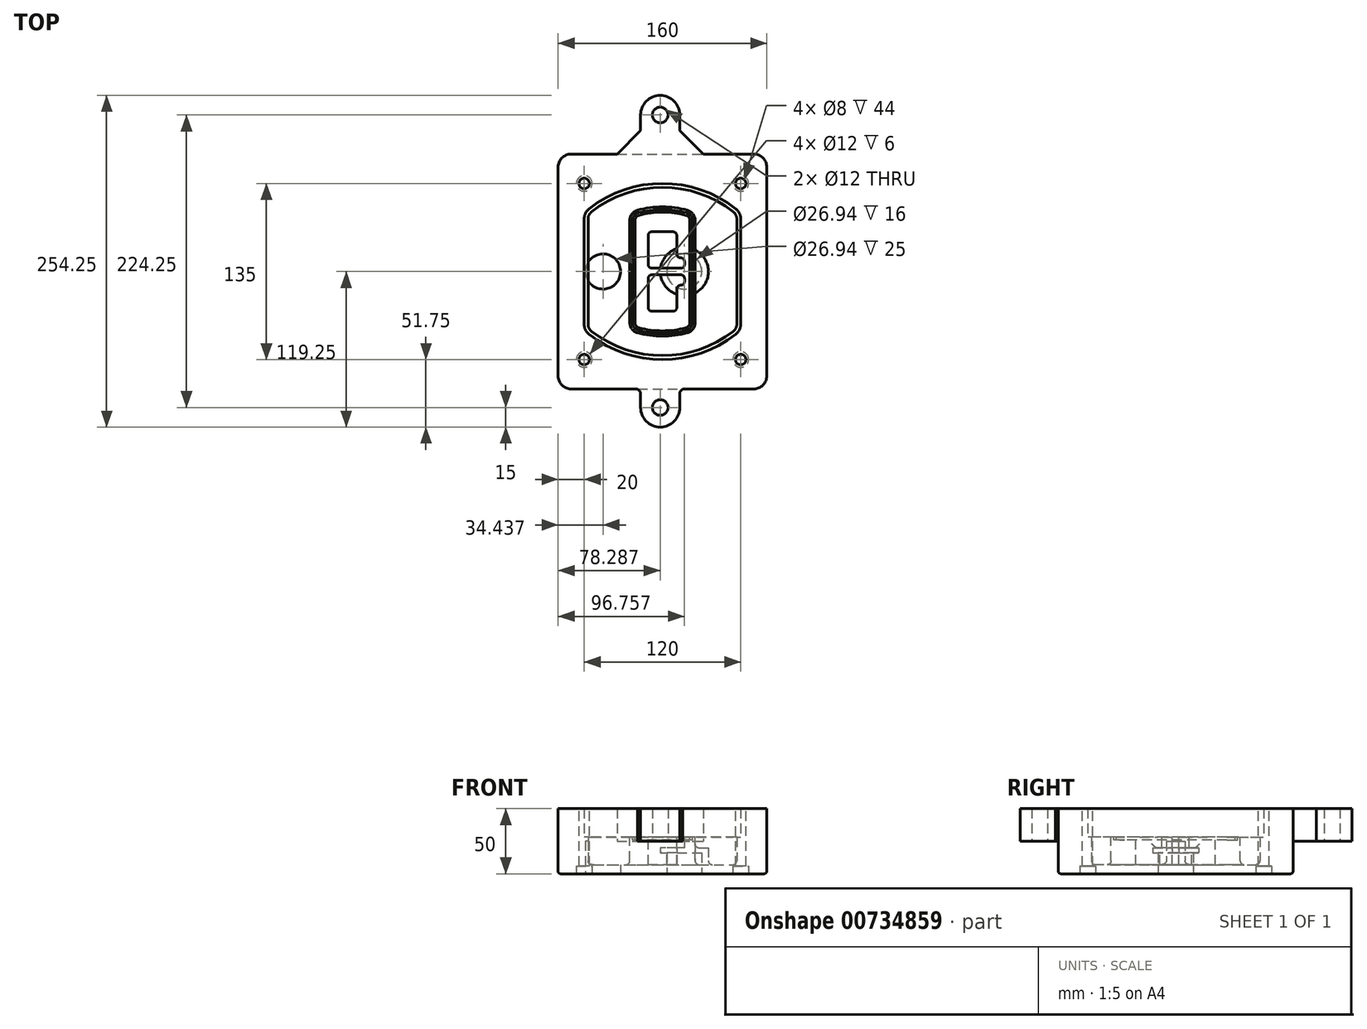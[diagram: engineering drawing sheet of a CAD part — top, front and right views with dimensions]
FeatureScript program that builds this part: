
annotation { "Feature Type Name" : "Feature", "Feature Type Description" : "" }
export const myFeature = defineFeature(function(context is Context, id is Id, definition is map)
    precondition{}
    {
        {
            var Q0;
            Q0=qCreatedBy(makeId("Top.planeOp"),FACE);
            var sketch = newSketch(context, id + "F0", { "sketchPlane" : qUnion([Q0])});
            skPoint(sketch, "E0.rect.middle", {"position": v(0, 0) * mm});
            skLineSegment(sketch, "E1.bottom", {"start": v(-70, -90) * mm, "end": v(70, -90) * mm});
            skLineSegment(sketch, "E1.top", {"start": v(-70, 90) * mm, "end": v(70, 90) * mm});
            skLineSegment(sketch, "E1.left", {"start": v(-80, -80) * mm, "end": v(-80, 80) * mm});
            skLineSegment(sketch, "E1.right", {"start": v(80, -80) * mm, "end": v(80, 80) * mm});
            skLineSegment(sketch, "E2", {"start": v(-80, 90) * mm, "end": v(80, -90) * mm, "construction": true});
            skLineSegment(sketch, "E3", {"start": v(80, 90) * mm, "end": v(-80, -90) * mm, "construction": true});
            skCircle(sketch, "E4", {"center": v(-60, 67.5) * mm, "radius": 4 * mm});
            skCircle(sketch, "E5", {"center": v(60, 67.5) * mm, "radius": 4 * mm});
            skCircle(sketch, "E6", {"center": v(60, -67.5) * mm, "radius": 4 * mm});
            skCircle(sketch, "E7", {"center": v(-60, -67.5) * mm, "radius": 4 * mm});
            skLineSegment(sketch, "E8", {"start": v(-60, 67.5) * mm, "end": v(60, 67.5) * mm, "construction": true});
            skLineSegment(sketch, "E9", {"start": v(60, 67.5) * mm, "end": v(60, -67.5) * mm, "construction": true});
            skLineSegment(sketch, "E10", {"start": v(60, -67.5) * mm, "end": v(-60, -67.5) * mm, "construction": true});
            skLineSegment(sketch, "E11", {"start": v(-60, -67.5) * mm, "end": v(-60, 67.5) * mm, "construction": true});
            skLineSegment(sketch, "E12", {"start": v(-60, 40.3) * mm, "end": v(-60, -40.3) * mm});
            skLineSegment(sketch, "E13", {"start": v(60, 40.3) * mm, "end": v(60, -40.3) * mm});
            skArc(sketch, "E14", {"start": v(56.15, 48.18) * mm, "mid": v(0, 67.5) * mm, "end": v(-56.15, 48.18) * mm});
            skArc(sketch, "E15", {"start": v(-56.15, -48.18) * mm, "mid": v(0, -67.5) * mm, "end": v(56.15, -48.18) * mm});
            skLineSegment(sketch, "E16", {"start": v(-60, 0) * mm, "end": v(60, 0) * mm, "construction": true});
            skPoint(sketch, "E17.visualSharp", {"position": v(-60, -45) * mm});
            skArc(sketch, "E17.filletArc", {"start": v(-60, -40.3) * mm, "mid": v(-58.99, -44.68) * mm, "end": v(-56.15, -48.18) * mm});
            skPoint(sketch, "E18.visualSharp", {"position": v(-60, 45) * mm});
            skArc(sketch, "E18.filletArc", {"start": v(-56.15, 48.18) * mm, "mid": v(-58.99, 44.68) * mm, "end": v(-60, 40.3) * mm});
            skPoint(sketch, "E19.visualSharp", {"position": v(60, 45) * mm});
            skArc(sketch, "E19.filletArc", {"start": v(60, 40.3) * mm, "mid": v(58.99, 44.68) * mm, "end": v(56.15, 48.18) * mm});
            skPoint(sketch, "E20.visualSharp", {"position": v(60, -45) * mm});
            skArc(sketch, "E20.filletArc", {"start": v(56.15, -48.18) * mm, "mid": v(58.99, -44.68) * mm, "end": v(60, -40.3) * mm});
            skPoint(sketch, "E21.visualSharp", {"position": v(-80, 90) * mm});
            skArc(sketch, "E21.filletArc", {"start": v(-70, 90) * mm, "mid": v(-77.07, 87.07) * mm, "end": v(-80, 80) * mm});
            skPoint(sketch, "E22.visualSharp", {"position": v(80, 90) * mm});
            skArc(sketch, "E22.filletArc", {"start": v(80, 80) * mm, "mid": v(77.07, 87.07) * mm, "end": v(70, 90) * mm});
            skPoint(sketch, "E23.visualSharp", {"position": v(80, -90) * mm});
            skArc(sketch, "E23.filletArc", {"start": v(70, -90) * mm, "mid": v(77.07, -87.07) * mm, "end": v(80, -80) * mm});
            skPoint(sketch, "E24.visualSharp", {"position": v(-80, -90) * mm});
            skArc(sketch, "E24.filletArc", {"start": v(-80, -80) * mm, "mid": v(-77.07, -87.07) * mm, "end": v(-70, -90) * mm});
            skArc(sketch, "E25.0", {"start": v(57, 40.3) * mm, "mid": v(56.3, 43.36) * mm, "end": v(54.3, 45.81) * mm});
            skLineSegment(sketch, "E25.1", {"start": v(57, 40.3) * mm, "end": v(57, -40.3) * mm});
            skArc(sketch, "E25.2", {"start": v(54.3, -45.81) * mm, "mid": v(56.3, -43.36) * mm, "end": v(57, -40.3) * mm});
            skArc(sketch, "E25.3", {"start": v(-54.3, -45.81) * mm, "mid": v(0, -64.5) * mm, "end": v(54.3, -45.81) * mm});
            skArc(sketch, "E25.4", {"start": v(-57, -40.3) * mm, "mid": v(-56.3, -43.36) * mm, "end": v(-54.3, -45.81) * mm});
            skArc(sketch, "E25.5", {"start": v(54.3, 45.81) * mm, "mid": v(0, 64.5) * mm, "end": v(-54.3, 45.81) * mm});
            skLineSegment(sketch, "E25.6", {"start": v(-57, 40.3) * mm, "end": v(-57, -40.3) * mm});
            skArc(sketch, "E25.7", {"start": v(-54.3, 45.81) * mm, "mid": v(-56.3, 43.36) * mm, "end": v(-57, 40.3) * mm});
            skArc(sketch, "E26.0", {"start": v(-58.62, 51.33) * mm, "mid": v(-62.58, 46.43) * mm, "end": v(-64, 40.3) * mm});
            skArc(sketch, "E26.1", {"start": v(58.62, 51.33) * mm, "mid": v(0, 71.5) * mm, "end": v(-58.62, 51.33) * mm});
            skArc(sketch, "E26.2", {"start": v(64, 40.3) * mm, "mid": v(62.58, 46.43) * mm, "end": v(58.62, 51.33) * mm});
            skLineSegment(sketch, "E26.3", {"start": v(64, 40.3) * mm, "end": v(64, -40.3) * mm});
            skArc(sketch, "E26.4", {"start": v(58.62, -51.33) * mm, "mid": v(62.58, -46.43) * mm, "end": v(64, -40.3) * mm});
            skLineSegment(sketch, "E26.5", {"start": v(-64, 40.3) * mm, "end": v(-64, -40.3) * mm});
            skArc(sketch, "E26.6", {"start": v(-58.62, -51.33) * mm, "mid": v(0, -71.5) * mm, "end": v(58.62, -51.33) * mm});
            skArc(sketch, "E26.7", {"start": v(-64, -40.3) * mm, "mid": v(-62.58, -46.43) * mm, "end": v(-58.62, -51.33) * mm});
            skSolve(sketch);
        }
        {
            var Q0;
            Q0=makeQuery(id+"F0.imprint","IMPRINT",FACE,{"disambiguationData":[TD([[makeQuery(id+"F0.imprint","IMPRINT",EDGE,{"derivedFrom":sQuery(id+"F0.wireOp",EDGE,"E1.bottom")}),1.0]])]});
            var Q1;
            Q1=makeQuery(id+"F0.imprint","IMPRINT",FACE,{"disambiguationData":[TD([[makeQuery(id+"F0.imprint","IMPRINT",EDGE,{"derivedFrom":sQuery(id+"F0.wireOp",EDGE,"E12")}),1.0]])]});
            var Q2;
            Q2=makeQuery(id+"F0.imprint","IMPRINT",FACE,{"disambiguationData":[TD([[makeQuery(id+"F0.imprint","IMPRINT",EDGE,{"derivedFrom":sQuery(id+"F0.wireOp",EDGE,"E25.0")}),1.0]])]});
            var Q3;
            Q3=makeQuery(id+"F0.imprint","IMPRINT",FACE,{"disambiguationData":[TD([[makeQuery(id+"F0.imprint","IMPRINT",EDGE,{"derivedFrom":sQuery(id+"F0.wireOp",EDGE,"E12")}),-1.0]])]});
            extrude(context, id + "F1", {"entities" : qUnion([Q0, Q1, Q2, Q3]), "oppositeDirection" : true, "depth" : 25 * mm});
        }
        {
            var Q0;
            Q0=makeQuery(id+"F0.imprint","IMPRINT",FACE,{"disambiguationData":[TD([[makeQuery(id+"F0.imprint","IMPRINT",EDGE,{"derivedFrom":sQuery(id+"F0.wireOp",EDGE,"E12")}),1.0]])]});
            extrude(context, id + "F2", {"entities" : qUnion([Q0]), "operationType" : NewBodyOperationType.ADD, "depth" : 3 * mm});
        }
        {
            var Q0;
            Q0=makeQuery(id+"F0.imprint","IMPRINT",FACE,{"disambiguationData":[TD([[makeQuery(id+"F0.imprint","IMPRINT",EDGE,{"derivedFrom":sQuery(id+"F0.wireOp",EDGE,"E25.0")}),1.0]])]});
            extrude(context, id + "F3", {"entities" : qUnion([Q0]), "operationType" : NewBodyOperationType.REMOVE, "oppositeDirection" : true, "depth" : 18 * mm});
        }
        {
            var Q0;
            Q0=makeQuery(id+"F2.opExtrude","CAP_FACE",FACE,{"disambiguationData":[OSD([sQuery(id+"F0.wireOp",EDGE,"E12"),sQuery(id+"F0.wireOp",EDGE,"E13"),sQuery(id+"F0.wireOp",EDGE,"E14"),sQuery(id+"F0.wireOp",EDGE,"E15"),sQuery(id+"F0.wireOp",EDGE,"E17.filletArc"),sQuery(id+"F0.wireOp",EDGE,"E18.filletArc"),sQuery(id+"F0.wireOp",EDGE,"E19.filletArc"),sQuery(id+"F0.wireOp",EDGE,"E20.filletArc"),sQuery(id+"F0.wireOp",EDGE,"E25.0"),sQuery(id+"F0.wireOp",EDGE,"E25.1"),sQuery(id+"F0.wireOp",EDGE,"E25.2"),sQuery(id+"F0.wireOp",EDGE,"E25.3"),sQuery(id+"F0.wireOp",EDGE,"E25.4"),sQuery(id+"F0.wireOp",EDGE,"E25.5"),sQuery(id+"F0.wireOp",EDGE,"E25.6"),sQuery(id+"F0.wireOp",EDGE,"E25.7")])],"isStart":false});
            var sketch = newSketch(context, id + "F4", { "sketchPlane" : qUnion([Q0])});
            skArc(sketch, "E27.0", {"start": v(-19.08, -46.97) * mm, "mid": v(0, -49.5) * mm, "end": v(19.08, -46.97) * mm});
            skArc(sketch, "E28.0", {"start": v(19.08, 46.97) * mm, "mid": v(0, 49.5) * mm, "end": v(-19.08, 46.97) * mm});
            skLineSegment(sketch, "E29", {"start": v(-25, 39.25) * mm, "end": v(-25, -39.25) * mm});
            skLineSegment(sketch, "E30", {"start": v(25, 39.25) * mm, "end": v(25, -39.25) * mm});
            skLineSegment(sketch, "E31", {"start": v(-25, 45.1) * mm, "end": v(25, 45.1) * mm, "construction": true});
            skLineSegment(sketch, "E32", {"start": v(-25, -45.1) * mm, "end": v(25, -45.1) * mm, "construction": true});
            skPoint(sketch, "E33.visualSharp", {"position": v(-25, 45.1) * mm});
            skArc(sketch, "E33.filletArc", {"start": v(-19.08, 46.97) * mm, "mid": v(-23.35, 44.11) * mm, "end": v(-25, 39.25) * mm});
            skPoint(sketch, "E34.visualSharp", {"position": v(25, 45.1) * mm});
            skArc(sketch, "E34.filletArc", {"start": v(25, 39.25) * mm, "mid": v(23.35, 44.11) * mm, "end": v(19.08, 46.97) * mm});
            skPoint(sketch, "E35.visualSharp", {"position": v(25, -45.1) * mm});
            skArc(sketch, "E35.filletArc", {"start": v(19.08, -46.97) * mm, "mid": v(23.35, -44.11) * mm, "end": v(25, -39.25) * mm});
            skPoint(sketch, "E36.visualSharp", {"position": v(-25, -45.1) * mm});
            skArc(sketch, "E36.filletArc", {"start": v(-25, -39.25) * mm, "mid": v(-23.35, -44.11) * mm, "end": v(-19.08, -46.97) * mm});
            skArc(sketch, "E37.0", {"start": v(54.3, 45.81) * mm, "mid": v(0, 64.5) * mm, "end": v(-54.3, 45.81) * mm});
            skArc(sketch, "E37.1", {"start": v(-54.3, 45.81) * mm, "mid": v(-56.3, 43.36) * mm, "end": v(-57, 40.3) * mm});
            skLineSegment(sketch, "E37.2", {"start": v(-57, 40.3) * mm, "end": v(-57, -40.3) * mm});
            skArc(sketch, "E37.3", {"start": v(-57, -40.3) * mm, "mid": v(-56.3, -43.36) * mm, "end": v(-54.3, -45.81) * mm});
            skArc(sketch, "E37.4", {"start": v(-54.3, -45.81) * mm, "mid": v(0, -64.5) * mm, "end": v(54.3, -45.81) * mm});
            skArc(sketch, "E37.5", {"start": v(54.3, -45.81) * mm, "mid": v(56.3, -43.36) * mm, "end": v(57, -40.3) * mm});
            skLineSegment(sketch, "E37.6", {"start": v(57, 40.3) * mm, "end": v(57, -40.3) * mm});
            skArc(sketch, "E37.7", {"start": v(57, 40.3) * mm, "mid": v(56.3, 43.36) * mm, "end": v(54.3, 45.81) * mm});
            skLineSegment(sketch, "E38.0", {"start": v(23, 39.25) * mm, "end": v(23, -39.25) * mm});
            skArc(sketch, "E38.1", {"start": v(18.56, -45.04) * mm, "mid": v(21.76, -42.9) * mm, "end": v(23, -39.25) * mm});
            skArc(sketch, "E38.2", {"start": v(-18.56, -45.04) * mm, "mid": v(0, -47.5) * mm, "end": v(18.56, -45.04) * mm});
            skArc(sketch, "E38.3", {"start": v(-23, -39.25) * mm, "mid": v(-21.76, -42.9) * mm, "end": v(-18.56, -45.04) * mm});
            skLineSegment(sketch, "E38.4", {"start": v(-23, 39.25) * mm, "end": v(-23, -39.25) * mm});
            skArc(sketch, "E38.5", {"start": v(23, 39.25) * mm, "mid": v(21.76, 42.9) * mm, "end": v(18.56, 45.04) * mm});
            skArc(sketch, "E38.6", {"start": v(-18.56, 45.04) * mm, "mid": v(-21.76, 42.9) * mm, "end": v(-23, 39.25) * mm});
            skArc(sketch, "E38.7", {"start": v(18.56, 45.04) * mm, "mid": v(0, 47.5) * mm, "end": v(-18.56, 45.04) * mm});
            skArc(sketch, "E39.0", {"start": v(21, 39.25) * mm, "mid": v(20.18, 41.68) * mm, "end": v(18.04, 43.1) * mm});
            skLineSegment(sketch, "E39.1", {"start": v(21, 39.25) * mm, "end": v(21, -39.25) * mm});
            skArc(sketch, "E39.2", {"start": v(18.04, -43.1) * mm, "mid": v(20.18, -41.68) * mm, "end": v(21, -39.25) * mm});
            skArc(sketch, "E39.3", {"start": v(-18.04, -43.1) * mm, "mid": v(0, -45.5) * mm, "end": v(18.04, -43.1) * mm});
            skArc(sketch, "E39.4", {"start": v(-21, -39.25) * mm, "mid": v(-20.18, -41.68) * mm, "end": v(-18.04, -43.1) * mm});
            skArc(sketch, "E39.5", {"start": v(18.04, 43.1) * mm, "mid": v(0, 45.5) * mm, "end": v(-18.04, 43.1) * mm});
            skLineSegment(sketch, "E39.6", {"start": v(-21, 39.25) * mm, "end": v(-21, -39.25) * mm});
            skArc(sketch, "E39.7", {"start": v(-18.04, 43.1) * mm, "mid": v(-20.18, 41.68) * mm, "end": v(-21, 39.25) * mm});
            skLineSegment(sketch, "E40", {"start": v(-25, 0) * mm, "end": v(25, 0) * mm, "construction": true});
            skLineSegment(sketch, "E41", {"start": v(-11, 5.5) * mm, "end": v(-11, 27.5) * mm});
            skLineSegment(sketch, "E42", {"start": v(-8, 30.5) * mm, "end": v(8, 30.5) * mm});
            skLineSegment(sketch, "E43", {"start": v(11, 27.5) * mm, "end": v(11, 13.5) * mm});
            skLineSegment(sketch, "E44", {"start": v(14, 10.5) * mm, "end": v(14, 10.5) * mm});
            skLineSegment(sketch, "E45", {"start": v(17, 7.5) * mm, "end": v(17, 5.5) * mm});
            skLineSegment(sketch, "E46", {"start": v(14, 2.5) * mm, "end": v(-8, 2.5) * mm});
            skPoint(sketch, "E47.visualSharp", {"position": v(-11, 30.5) * mm});
            skArc(sketch, "E47.filletArc", {"start": v(-8, 30.5) * mm, "mid": v(-10.12, 29.62) * mm, "end": v(-11, 27.5) * mm});
            skPoint(sketch, "E48.visualSharp", {"position": v(11, 30.5) * mm});
            skArc(sketch, "E48.filletArc", {"start": v(11, 27.5) * mm, "mid": v(10.12, 29.62) * mm, "end": v(8, 30.5) * mm});
            skPoint(sketch, "E49.visualSharp", {"position": v(11, 10.5) * mm});
            skArc(sketch, "E49.filletArc", {"start": v(11, 13.5) * mm, "mid": v(11.88, 11.38) * mm, "end": v(14, 10.5) * mm});
            skPoint(sketch, "E50.visualSharp", {"position": v(17, 10.5) * mm});
            skArc(sketch, "E50.filletArc", {"start": v(17, 7.5) * mm, "mid": v(16.12, 9.62) * mm, "end": v(14, 10.5) * mm});
            skPoint(sketch, "E51.visualSharp", {"position": v(17, 2.5) * mm});
            skArc(sketch, "E51.filletArc", {"start": v(14, 2.5) * mm, "mid": v(16.12, 3.38) * mm, "end": v(17, 5.5) * mm});
            skPoint(sketch, "E52.visualSharp", {"position": v(-11, 2.5) * mm});
            skArc(sketch, "E52.filletArc", {"start": v(-11, 5.5) * mm, "mid": v(-10.12, 3.38) * mm, "end": v(-8, 2.5) * mm});
            skLineSegment(sketch, "E53.0.MirrorCS", {"start": v(14, -2.5) * mm, "end": v(-8, -2.5) * mm});
            skArc(sketch, "E54.0.MirrorCS", {"start": v(-11, -5.5) * mm, "mid": v(-10.12, -3.38) * mm, "end": v(-8, -2.5) * mm});
            skLineSegment(sketch, "E55.0.MirrorCS", {"start": v(-11, -5.5) * mm, "end": v(-11, -27.5) * mm});
            skArc(sketch, "E56.0.MirrorCS", {"start": v(-8, -30.5) * mm, "mid": v(-10.12, -29.62) * mm, "end": v(-11, -27.5) * mm});
            skLineSegment(sketch, "E57.0.MirrorCS", {"start": v(-8, -30.5) * mm, "end": v(8, -30.5) * mm});
            skArc(sketch, "E58.0.MirrorCS", {"start": v(11, -27.5) * mm, "mid": v(10.12, -29.62) * mm, "end": v(8, -30.5) * mm});
            skLineSegment(sketch, "E59.0.MirrorCS", {"start": v(11, -27.5) * mm, "end": v(11, -13.5) * mm});
            skArc(sketch, "E60.0.MirrorCS", {"start": v(11, -13.5) * mm, "mid": v(11.88, -11.38) * mm, "end": v(14, -10.5) * mm});
            skArc(sketch, "E61.0.MirrorCS", {"start": v(17, -7.5) * mm, "mid": v(16.12, -9.62) * mm, "end": v(14, -10.5) * mm});
            skLineSegment(sketch, "E62.0.MirrorCS", {"start": v(17, -7.5) * mm, "end": v(17, -5.5) * mm});
            skArc(sketch, "E63.0.MirrorCS", {"start": v(14, -2.5) * mm, "mid": v(16.12, -3.38) * mm, "end": v(17, -5.5) * mm});
            skSolve(sketch);
        }
        {
            var Q0;
            Q0=makeQuery(id+"F4.imprint","IMPRINT",FACE,{"disambiguationData":[TD([[makeQuery(id+"F4.imprint","IMPRINT",EDGE,{"derivedFrom":sQuery(id+"F4.wireOp",EDGE,"E27.0")}),1.0]])]});
            var Q1;
            Q1=makeQuery(id+"F4.imprint","IMPRINT",FACE,{"disambiguationData":[TD([[makeQuery(id+"F4.imprint","IMPRINT",EDGE,{"derivedFrom":sQuery(id+"F4.wireOp",EDGE,"E38.0")}),-1.0]])]});
            var Q2;
            Q2=makeQuery(id+"F4.imprint","IMPRINT",FACE,{"disambiguationData":[TD([[makeQuery(id+"F4.imprint","IMPRINT",EDGE,{"derivedFrom":sQuery(id+"F4.wireOp",EDGE,"E39.0")}),1.0]])]});
            extrude(context, id + "F5", {"entities" : qUnion([Q0, Q1, Q2]), "operationType" : NewBodyOperationType.ADD, "endBound" : BoundingType.UP_TO_NEXT, "oppositeDirection" : true, "depth" : 25 * mm});
        }
        {
            var Q0;
            Q0=makeQuery(id+"F4.imprint","IMPRINT",FACE,{"disambiguationData":[TD([[makeQuery(id+"F4.imprint","IMPRINT",EDGE,{"derivedFrom":sQuery(id+"F4.wireOp",EDGE,"E38.0")}),-1.0]])]});
            extrude(context, id + "F6", {"entities" : qUnion([Q0]), "operationType" : NewBodyOperationType.REMOVE, "oppositeDirection" : true, "depth" : 2 * mm});
        }
        {
            var Q0;
            Q0=makeQuery(id+"F1.opExtrude","CAP_FACE",FACE,{"disambiguationData":[OSD([sQuery(id+"F0.wireOp",EDGE,"E1.bottom"),sQuery(id+"F0.wireOp",EDGE,"E1.top"),sQuery(id+"F0.wireOp",EDGE,"E1.left"),sQuery(id+"F0.wireOp",EDGE,"E1.right"),sQuery(id+"F0.wireOp",EDGE,"E4"),sQuery(id+"F0.wireOp",EDGE,"E5"),sQuery(id+"F0.wireOp",EDGE,"E6"),sQuery(id+"F0.wireOp",EDGE,"E7"),sQuery(id+"F0.wireOp",EDGE,"E21.filletArc"),sQuery(id+"F0.wireOp",EDGE,"E22.filletArc"),sQuery(id+"F0.wireOp",EDGE,"E23.filletArc"),sQuery(id+"F0.wireOp",EDGE,"E24.filletArc")])],"isStart":false});
            var sketch = newSketch(context, id + "F7", { "sketchPlane" : qUnion([Q0])});
            skCircle(sketch, "E64", {"center": v(16.76, 0) * mm, "radius": 13.47 * mm});
            skCircle(sketch, "E65", {"center": v(-45.56, 0) * mm, "radius": 13.47 * mm});
            skLineSegment(sketch, "E66", {"start": v(80, 0) * mm, "end": v(-80, 0) * mm});
            skCircle(sketch, "E67", {"center": v(16.76, 0) * mm, "radius": 18.47 * mm});
            skCircle(sketch, "E68", {"center": v(60, -67.5) * mm, "radius": 6 * mm});
            skCircle(sketch, "E69", {"center": v(-60, -67.5) * mm, "radius": 6 * mm});
            skCircle(sketch, "E70", {"center": v(-60, 67.5) * mm, "radius": 6 * mm});
            skCircle(sketch, "E71", {"center": v(60, 67.5) * mm, "radius": 6 * mm});
            skSolve(sketch);
        }
        {
            var Q0;
            {var subQ1=sQuery(id+"F7.wireOp",EDGE,"E66");var subQ4=sQuery(id+"F7.wireOp",EDGE,"E64");var subQ6=makeQuery(id+"F7.imprint","INTERSECT",VERTEX,{"disambiguationData":[OD(0.0)],"derivedFrom":[subQ4,subQ1]});Q0=makeQuery(id+"F7.imprint","IMPRINT",FACE,{"disambiguationData":[TD([[makeQuery(id+"F7.imprint","IMPRINT",EDGE,{"disambiguationData":[TD([[subQ6,-1.0]])],"derivedFrom":subQ4}),-1.0]])]});}
            var Q1;
            {var subQ0=sQuery(id+"F7.wireOp",EDGE,"E66");var subQ1=sQuery(id+"F7.wireOp",EDGE,"E64");var subQ3=makeQuery(id+"F7.imprint","INTERSECT",VERTEX,{"disambiguationData":[OD(0.0)],"derivedFrom":[subQ1,subQ0]});Q1=makeQuery(id+"F7.imprint","IMPRINT",FACE,{"disambiguationData":[TD([[makeQuery(id+"F7.imprint","IMPRINT",EDGE,{"disambiguationData":[TD([[subQ3,-1.0]])],"derivedFrom":subQ1}),1.0]])]});}
            var Q2;
            {var subQ0=sQuery(id+"F7.wireOp",EDGE,"E66");var subQ1=sQuery(id+"F7.wireOp",EDGE,"E64");var subQ3=makeQuery(id+"F7.imprint","INTERSECT",VERTEX,{"disambiguationData":[OD(0.0)],"derivedFrom":[subQ1,subQ0]});Q2=makeQuery(id+"F7.imprint","IMPRINT",FACE,{"disambiguationData":[TD([[makeQuery(id+"F7.imprint","IMPRINT",EDGE,{"disambiguationData":[TD([[subQ3,1.0]])],"derivedFrom":subQ1}),1.0]])]});}
            var Q3;
            {var subQ1=sQuery(id+"F7.wireOp",EDGE,"E66");var subQ4=sQuery(id+"F7.wireOp",EDGE,"E64");var subQ6=makeQuery(id+"F7.imprint","INTERSECT",VERTEX,{"disambiguationData":[OD(0.0)],"derivedFrom":[subQ4,subQ1]});Q3=makeQuery(id+"F7.imprint","IMPRINT",FACE,{"disambiguationData":[TD([[makeQuery(id+"F7.imprint","IMPRINT",EDGE,{"disambiguationData":[TD([[subQ6,1.0]])],"derivedFrom":subQ4}),-1.0]])]});}
            extrude(context, id + "F8", {"entities" : qUnion([Q0, Q1, Q2, Q3]), "operationType" : NewBodyOperationType.ADD, "oppositeDirection" : true, "depth" : 20 * mm});
        }
        {
            var Q0;
            {var subQ0=sQuery(id+"F7.wireOp",EDGE,"E66");var subQ1=sQuery(id+"F7.wireOp",EDGE,"E64");var subQ3=makeQuery(id+"F7.imprint","INTERSECT",VERTEX,{"disambiguationData":[OD(0.0)],"derivedFrom":[subQ1,subQ0]});Q0=makeQuery(id+"F7.imprint","IMPRINT",FACE,{"disambiguationData":[TD([[makeQuery(id+"F7.imprint","IMPRINT",EDGE,{"disambiguationData":[TD([[subQ3,-1.0]])],"derivedFrom":subQ1}),1.0]])]});}
            var Q1;
            {var subQ0=sQuery(id+"F7.wireOp",EDGE,"E66");var subQ1=sQuery(id+"F7.wireOp",EDGE,"E64");var subQ3=makeQuery(id+"F7.imprint","INTERSECT",VERTEX,{"disambiguationData":[OD(0.0)],"derivedFrom":[subQ1,subQ0]});Q1=makeQuery(id+"F7.imprint","IMPRINT",FACE,{"disambiguationData":[TD([[makeQuery(id+"F7.imprint","IMPRINT",EDGE,{"disambiguationData":[TD([[subQ3,1.0]])],"derivedFrom":subQ1}),1.0]])]});}
            extrude(context, id + "F9", {"entities" : qUnion([Q0, Q1]), "operationType" : NewBodyOperationType.REMOVE, "oppositeDirection" : true, "depth" : 16 * mm});
        }
        {
            var Q0;
            {var subQ0=sQuery(id+"F7.wireOp",EDGE,"E66");var subQ1=sQuery(id+"F7.wireOp",EDGE,"E65");var subQ3=makeQuery(id+"F7.imprint","INTERSECT",VERTEX,{"disambiguationData":[OD(0.0)],"derivedFrom":[subQ1,subQ0]});Q0=makeQuery(id+"F7.imprint","IMPRINT",FACE,{"disambiguationData":[TD([[makeQuery(id+"F7.imprint","IMPRINT",EDGE,{"disambiguationData":[TD([[subQ3,-1.0]])],"derivedFrom":subQ1}),1.0]])]});}
            var Q1;
            {var subQ0=sQuery(id+"F7.wireOp",EDGE,"E66");var subQ1=sQuery(id+"F7.wireOp",EDGE,"E65");var subQ3=makeQuery(id+"F7.imprint","INTERSECT",VERTEX,{"disambiguationData":[OD(0.0)],"derivedFrom":[subQ1,subQ0]});Q1=makeQuery(id+"F7.imprint","IMPRINT",FACE,{"disambiguationData":[TD([[makeQuery(id+"F7.imprint","IMPRINT",EDGE,{"disambiguationData":[TD([[subQ3,1.0]])],"derivedFrom":subQ1}),1.0]])]});}
            extrude(context, id + "F10", {"entities" : qUnion([Q0, Q1]), "operationType" : NewBodyOperationType.REMOVE, "oppositeDirection" : true, "depth" : 25 * mm});
        }
        {
            var Q0;
            Q0=makeQuery(id+"F7.imprint","IMPRINT",FACE,{"disambiguationData":[TD([[makeQuery(id+"F7.imprint","IMPRINT",EDGE,{"derivedFrom":sQuery(id+"F7.wireOp",EDGE,"E68")}),1.0]])]});
            var Q1;
            Q1=makeQuery(id+"F7.imprint","IMPRINT",FACE,{"disambiguationData":[TD([[makeQuery(id+"F7.imprint","IMPRINT",EDGE,{"derivedFrom":makeQuery(id+"F1.opExtrude","CAP_EDGE",EDGE,{"disambiguationData":[OSD([sQuery(id+"F0.wireOp",EDGE,"E5")])],"isStart":false})}),-1.0]])]});
            var Q2;
            Q2=makeQuery(id+"F7.imprint","IMPRINT",FACE,{"disambiguationData":[TD([[makeQuery(id+"F7.imprint","IMPRINT",EDGE,{"derivedFrom":sQuery(id+"F7.wireOp",EDGE,"E69")}),1.0]])]});
            var Q3;
            Q3=makeQuery(id+"F7.imprint","IMPRINT",FACE,{"disambiguationData":[TD([[makeQuery(id+"F7.imprint","IMPRINT",EDGE,{"derivedFrom":makeQuery(id+"F1.opExtrude","CAP_EDGE",EDGE,{"disambiguationData":[OSD([sQuery(id+"F0.wireOp",EDGE,"E4")])],"isStart":false})}),-1.0]])]});
            var Q4;
            Q4=makeQuery(id+"F7.imprint","IMPRINT",FACE,{"disambiguationData":[TD([[makeQuery(id+"F7.imprint","IMPRINT",EDGE,{"derivedFrom":sQuery(id+"F7.wireOp",EDGE,"E70")}),1.0]])]});
            var Q5;
            Q5=makeQuery(id+"F7.imprint","IMPRINT",FACE,{"disambiguationData":[TD([[makeQuery(id+"F7.imprint","IMPRINT",EDGE,{"derivedFrom":makeQuery(id+"F1.opExtrude","CAP_EDGE",EDGE,{"disambiguationData":[OSD([sQuery(id+"F0.wireOp",EDGE,"E7")])],"isStart":false})}),-1.0]])]});
            var Q6;
            Q6=makeQuery(id+"F7.imprint","IMPRINT",FACE,{"disambiguationData":[TD([[makeQuery(id+"F7.imprint","IMPRINT",EDGE,{"derivedFrom":sQuery(id+"F7.wireOp",EDGE,"E71")}),1.0]])]});
            var Q7;
            Q7=makeQuery(id+"F7.imprint","IMPRINT",FACE,{"disambiguationData":[TD([[makeQuery(id+"F7.imprint","IMPRINT",EDGE,{"derivedFrom":makeQuery(id+"F1.opExtrude","CAP_EDGE",EDGE,{"disambiguationData":[OSD([sQuery(id+"F0.wireOp",EDGE,"E6")])],"isStart":false})}),-1.0]])]});
            extrude(context, id + "F11", {"entities" : qUnion([Q0, Q1, Q2, Q3, Q4, Q5, Q6, Q7]), "operationType" : NewBodyOperationType.REMOVE, "oppositeDirection" : true, "depth" : 6 * mm});
        }
        {
            var Q0;
            Q0=makeQuery(id+"F9.boolean.opBoolean","COPY",FACE,{"derivedFrom":makeQuery(id+"F9.opExtrude","CAP_FACE",FACE,{"disambiguationData":[OSD([sQuery(id+"F7.wireOp",EDGE,"E64")])],"isStart":false})});
            var sketch = newSketch(context, id + "F12", { "sketchPlane" : qUnion([Q0])});
            skArc(sketch, "E72.0", {"start": v(11, 17.55) * mm, "mid": v(2.57, 11.82) * mm, "end": v(-1.54, 2.5) * mm});
            skArc(sketch, "E72.1", {"start": v(-1.54, -2.5) * mm, "mid": v(2.57, -11.82) * mm, "end": v(11, -17.55) * mm});
            skLineSegment(sketch, "E73", {"start": v(-1.54, -2.5) * mm, "end": v(14, -2.5) * mm});
            skLineSegment(sketch, "E74.0", {"start": v(14, 2.5) * mm, "end": v(-1.54, 2.5) * mm});
            skArc(sketch, "E74.1", {"start": v(14, 2.5) * mm, "mid": v(16.12, 3.38) * mm, "end": v(17, 5.5) * mm});
            skLineSegment(sketch, "E74.2", {"start": v(17, 7.5) * mm, "end": v(17, 5.5) * mm});
            skArc(sketch, "E74.3", {"start": v(17, 7.5) * mm, "mid": v(16.12, 9.62) * mm, "end": v(14, 10.5) * mm});
            skArc(sketch, "E74.4", {"start": v(11, 13.5) * mm, "mid": v(11.88, 11.38) * mm, "end": v(14, 10.5) * mm});
            skLineSegment(sketch, "E74.5", {"start": v(11, 17.55) * mm, "end": v(11, 13.5) * mm});
            skLineSegment(sketch, "E74.7", {"start": v(14, -2.5) * mm, "end": v(-1.54, -2.5) * mm});
            skArc(sketch, "E74.8", {"start": v(14, -2.5) * mm, "mid": v(16.12, -3.38) * mm, "end": v(17, -5.5) * mm});
            skLineSegment(sketch, "E74.9", {"start": v(17, -7.5) * mm, "end": v(17, -5.5) * mm});
            skArc(sketch, "E74.10", {"start": v(17, -7.5) * mm, "mid": v(16.12, -9.62) * mm, "end": v(14, -10.5) * mm});
            skArc(sketch, "E74.11", {"start": v(11, -13.5) * mm, "mid": v(11.88, -11.38) * mm, "end": v(14, -10.5) * mm});
            skLineSegment(sketch, "E74.12", {"start": v(11, -17.55) * mm, "end": v(11, -13.5) * mm});
            skPoint(sketch, "E75.orphan", {"position": v(11, -27.5) * mm});
            skPoint(sketch, "E76.orphan", {"position": v(-8, -2.5) * mm});
            skPoint(sketch, "E77.orphan", {"position": v(-8, 2.5) * mm});
            skPoint(sketch, "E78.orphan", {"position": v(11, 27.5) * mm});
            skSolve(sketch);
        }
        {
            var Q0;
            {var subQ7=sQuery(id+"F12.wireOp",EDGE,"E72.0");var subQ14=sQuery(id+"F12.wireOp",EDGE,"E72.1");var subQ16=sQuery(id+"F12.wireOp",EDGE,"E74.1");var subQ18=sQuery(id+"F12.wireOp",EDGE,"E74.8");Q0=qUnion([makeQuery(id+"F12.imprint","IMPRINT",FACE,{"disambiguationData":[TD([[makeQuery(id+"F12.imprint","IMPRINT",EDGE,{"derivedFrom":subQ7}),1.0]])]}),makeQuery(id+"F12.imprint","IMPRINT",FACE,{"disambiguationData":[TD([[makeQuery(id+"F12.imprint","IMPRINT",EDGE,{"derivedFrom":subQ14}),1.0]])]}),makeQuery(id+"F12.imprint","IMPRINT",FACE,{"disambiguationData":[TD([[makeQuery(id+"F12.imprint","IMPRINT",EDGE,{"derivedFrom":subQ16}),1.0]])]}),makeQuery(id+"F12.imprint","IMPRINT",FACE,{"disambiguationData":[TD([[makeQuery(id+"F12.imprint","IMPRINT",EDGE,{"derivedFrom":subQ18}),-1.0]])]})]);}
            var Q1;
            Q1=makeQuery(id+"F5.boolean.opBoolean","SPLIT",FACE,{"disambiguationData":[TD([makeQuery(id+"F5.opExtrude","SWEPT_FACE",FACE,{"disambiguationData":[OSD([sQuery(id+"F4.wireOp",EDGE,"E41")])]})])],"derivedFrom":makeQuery(id+"F3.boolean.opBoolean","COPY",FACE,{"derivedFrom":makeQuery(id+"F3.opExtrude","CAP_FACE",FACE,{"disambiguationData":[OSD([sQuery(id+"F0.wireOp",EDGE,"E25.0"),sQuery(id+"F0.wireOp",EDGE,"E25.1"),sQuery(id+"F0.wireOp",EDGE,"E25.2"),sQuery(id+"F0.wireOp",EDGE,"E25.3"),sQuery(id+"F0.wireOp",EDGE,"E25.4"),sQuery(id+"F0.wireOp",EDGE,"E25.5"),sQuery(id+"F0.wireOp",EDGE,"E25.6"),sQuery(id+"F0.wireOp",EDGE,"E25.7")])],"isStart":false})})});
            extrude(context, id + "F13", {"entities" : qUnion([Q0]), "operationType" : NewBodyOperationType.REMOVE, "endBound" : BoundingType.UP_TO_SURFACE, "endBoundEntityFace" : qUnion([Q1]), "depth" : 25 * mm});
        }
        {
            var Q0;
            Q0=makeQuery(id+"F3.boolean.opBoolean","COPY",EDGE,{"derivedFrom":makeQuery(id+"F3.opExtrude","CAP_EDGE",EDGE,{"disambiguationData":[OSD([sQuery(id+"F0.wireOp",EDGE,"E25.6")])],"isStart":false})});
            var Q1;
            Q1=makeQuery(id+"F8.boolean.opBoolean","INTERSECT",EDGE,{"derivedFrom":[makeQuery(id+"F5.opExtrude","SWEPT_FACE",FACE,{"disambiguationData":[OSD([sQuery(id+"F4.wireOp",EDGE,"E30")])]}),makeQuery(id+"F8.opExtrude","CAP_FACE",FACE,{"disambiguationData":[OSD([sQuery(id+"F7.wireOp",EDGE,"E67")])],"isStart":false})]});
            var Q2;
            Q2=makeQuery(id+"F8.boolean.opBoolean","INTERSECT",EDGE,{"disambiguationData":[OD(1.0)],"derivedFrom":[makeQuery(id+"F5.opExtrude","SWEPT_FACE",FACE,{"disambiguationData":[OSD([sQuery(id+"F4.wireOp",EDGE,"E30")])]}),makeQuery(id+"F8.opExtrude","SWEPT_FACE",FACE,{"disambiguationData":[OSD([sQuery(id+"F7.wireOp",EDGE,"E67")])]})]});
            var Q3;
            {var subQ0=sQuery(id+"F4.wireOp",EDGE,"E30");Q3=makeQuery(id+"F8.boolean.opBoolean","SPLIT",EDGE,{"disambiguationData":[TD([makeQuery(id+"F5.opExtrude","SWEPT_FACE",FACE,{"disambiguationData":[OSD([sQuery(id+"F4.wireOp",EDGE,"E35.filletArc")])]})])],"derivedFrom":makeQuery(id+"F5.opExtrude","CAP_EDGE",EDGE,{"disambiguationData":[OSD([subQ0])],"isStart":false})});}
            var Q4;
            {var subQ0=sQuery(id+"F0.wireOp",EDGE,"E25.7");var subQ1=sQuery(id+"F0.wireOp",EDGE,"E25.1");var subQ2=sQuery(id+"F0.wireOp",EDGE,"E25.6");var subQ3=sQuery(id+"F0.wireOp",EDGE,"E25.5");var subQ4=sQuery(id+"F0.wireOp",EDGE,"E25.4");var subQ5=sQuery(id+"F0.wireOp",EDGE,"E25.0");var subQ6=sQuery(id+"F0.wireOp",EDGE,"E25.2");var subQ7=sQuery(id+"F0.wireOp",EDGE,"E25.3");Q4=makeQuery(id+"F8.boolean.opBoolean","INTERSECT",EDGE,{"derivedFrom":[makeQuery(id+"F5.boolean.opBoolean","SPLIT",FACE,{"disambiguationData":[TD([makeQuery(id+"F2.opExtrude","SWEPT_FACE",FACE,{"disambiguationData":[OSD([subQ5])]})])],"derivedFrom":makeQuery(id+"F3.boolean.opBoolean","COPY",FACE,{"derivedFrom":makeQuery(id+"F3.opExtrude","CAP_FACE",FACE,{"disambiguationData":[OSD([subQ5,subQ1,subQ6,subQ7,subQ4,subQ3,subQ2,subQ0])],"isStart":false})})}),makeQuery(id+"F8.opExtrude","SWEPT_FACE",FACE,{"disambiguationData":[OSD([sQuery(id+"F7.wireOp",EDGE,"E67")])]})]});}
            var Q5;
            Q5=makeQuery(id+"F8.boolean.opBoolean","INTERSECT",EDGE,{"disambiguationData":[OD(0.0)],"derivedFrom":[makeQuery(id+"F5.opExtrude","SWEPT_FACE",FACE,{"disambiguationData":[OSD([sQuery(id+"F4.wireOp",EDGE,"E30")])]}),makeQuery(id+"F8.opExtrude","SWEPT_FACE",FACE,{"disambiguationData":[OSD([sQuery(id+"F7.wireOp",EDGE,"E67")])]})]});
            fillet(context, id + "F14", {"entities" : qUnion([Q0, Q1, Q2, Q3, Q4, Q5]), "radius" : 3 * mm, "tangentPropagation" : true, "allowEdgeOverflow" : false});
        }
        {
            var Q0;
            Q0=makeQuery(id+"F1.opExtrude","CAP_EDGE",EDGE,{"disambiguationData":[OSD([sQuery(id+"F0.wireOp",EDGE,"E1.bottom")])],"isStart":false});
            fillet(context, id + "F15", {"entities" : qUnion([Q0]), "radius" : 2 * mm, "tangentPropagation" : true, "allowEdgeOverflow" : false});
        }
        {
            var Q0;
            {var subQ0=sQuery(id+"F0.wireOp",EDGE,"E21.filletArc");var subQ1=sQuery(id+"F0.wireOp",EDGE,"E7");var subQ2=sQuery(id+"F0.wireOp",EDGE,"E6");var subQ3=sQuery(id+"F0.wireOp",EDGE,"E5");var subQ4=sQuery(id+"F0.wireOp",EDGE,"E4");var subQ5=sQuery(id+"F0.wireOp",EDGE,"E22.filletArc");var subQ6=sQuery(id+"F0.wireOp",EDGE,"E1.bottom");var subQ7=sQuery(id+"F0.wireOp",EDGE,"E1.right");var subQ8=sQuery(id+"F0.wireOp",EDGE,"E1.top");var subQ9=sQuery(id+"F0.wireOp",EDGE,"E1.left");var subQ10=sQuery(id+"F0.wireOp",EDGE,"E23.filletArc");var subQ11=sQuery(id+"F0.wireOp",EDGE,"E24.filletArc");Q0=makeQuery(id+"F2.boolean.opBoolean","SPLIT",FACE,{"disambiguationData":[TD([makeQuery(id+"F1.opExtrude","SWEPT_FACE",FACE,{"disambiguationData":[OSD([subQ6])]})])],"derivedFrom":makeQuery(id+"F1.opExtrude","CAP_FACE",FACE,{"disambiguationData":[OSD([subQ6,subQ8,subQ9,subQ7,subQ4,subQ3,subQ2,subQ1,subQ0,subQ5,subQ10,subQ11])],"isStart":true})});}
            var sketch = newSketch(context, id + "F16", { "sketchPlane" : qUnion([Q0])});
            skLineSegment(sketch, "E79", {"start": v(-34.71, 90) * mm, "end": v(-16.71, 108) * mm});
            skLineSegment(sketch, "E80", {"start": v(13.29, 108) * mm, "end": v(31.29, 90) * mm});
            skLineSegment(sketch, "E81", {"start": v(-16.71, 108) * mm, "end": v(-16.71, 120) * mm});
            skLineSegment(sketch, "E82", {"start": v(13.29, 108) * mm, "end": v(13.29, 120) * mm});
            skArc(sketch, "E83", {"start": v(13.29, 120) * mm, "mid": v(-1.71, 135) * mm, "end": v(-16.71, 120) * mm});
            skCircle(sketch, "E84", {"center": v(-1.71, 120) * mm, "radius": 6 * mm});
            skLineSegment(sketch, "E85", {"start": v(-1.71, 120) * mm, "end": v(-1.71, 90) * mm, "construction": true});
            skArc(sketch, "E86.MirrorCS", {"start": v(13.29, 104.25) * mm, "mid": v(-1.71, 119.25) * mm, "end": v(-16.71, 104.25) * mm});
            skLineSegment(sketch, "E87.MirrorCS", {"start": v(-34.71, -74.25) * mm, "end": v(-16.71, -92.25) * mm});
            skArc(sketch, "E88.MirrorCS", {"start": v(13.29, -104.25) * mm, "mid": v(-1.71, -119.25) * mm, "end": v(-16.71, -104.25) * mm});
            skLineSegment(sketch, "E89.MirrorCS", {"start": v(-16.71, -92.25) * mm, "end": v(-16.71, -104.25) * mm});
            skLineSegment(sketch, "E90.MirrorCS", {"start": v(-1.71, -104.25) * mm, "end": v(-1.71, -74.25) * mm, "construction": true});
            skLineSegment(sketch, "E91.MirrorCS", {"start": v(13.29, -92.25) * mm, "end": v(31.29, -74.25) * mm});
            skLineSegment(sketch, "E92.MirrorCS", {"start": v(13.29, -92.25) * mm, "end": v(13.29, -104.25) * mm});
            skCircle(sketch, "E93.MirrorC", {"center": v(-1.71, -104.25) * mm, "radius": 6 * mm});
            skSolve(sketch);
        }
        {
            var Q0;
            Q0=makeQuery(id+"F16.imprint","IMPRINT",FACE,{"disambiguationData":[TD([[makeQuery(id+"F16.imprint","IMPRINT",EDGE,{"derivedFrom":makeQuery(id+"F1.opExtrude","CAP_EDGE",EDGE,{"disambiguationData":[OSD([sQuery(id+"F0.wireOp",EDGE,"E1.left")])],"isStart":true})}),-1.0]])]});
            var Q1;
            {var subQ0=sQuery(id+"F16.wireOp",EDGE,"E79");Q1=makeQuery(id+"F16.imprint","IMPRINT",FACE,{"disambiguationData":[TD([[makeQuery(id+"F16.imprint","IMPRINT",EDGE,{"derivedFrom":subQ0}),-1.0]])]});}
            var Q2;
            {var subQ1=sQuery(id+"F16.wireOp",EDGE,"E87.MirrorCS");Q2=makeQuery(id+"F16.imprint","IMPRINT",FACE,{"disambiguationData":[TD([[makeQuery(id+"F16.imprint","IMPRINT",EDGE,{"derivedFrom":subQ1}),1.0]])]});}
            extrude(context, id + "F17", {"entities" : qUnion([Q0, Q1, Q2]), "operationType" : NewBodyOperationType.ADD, "depth" : 25 * mm, "offsetDistance" : 25 * mm});
        }
    });
